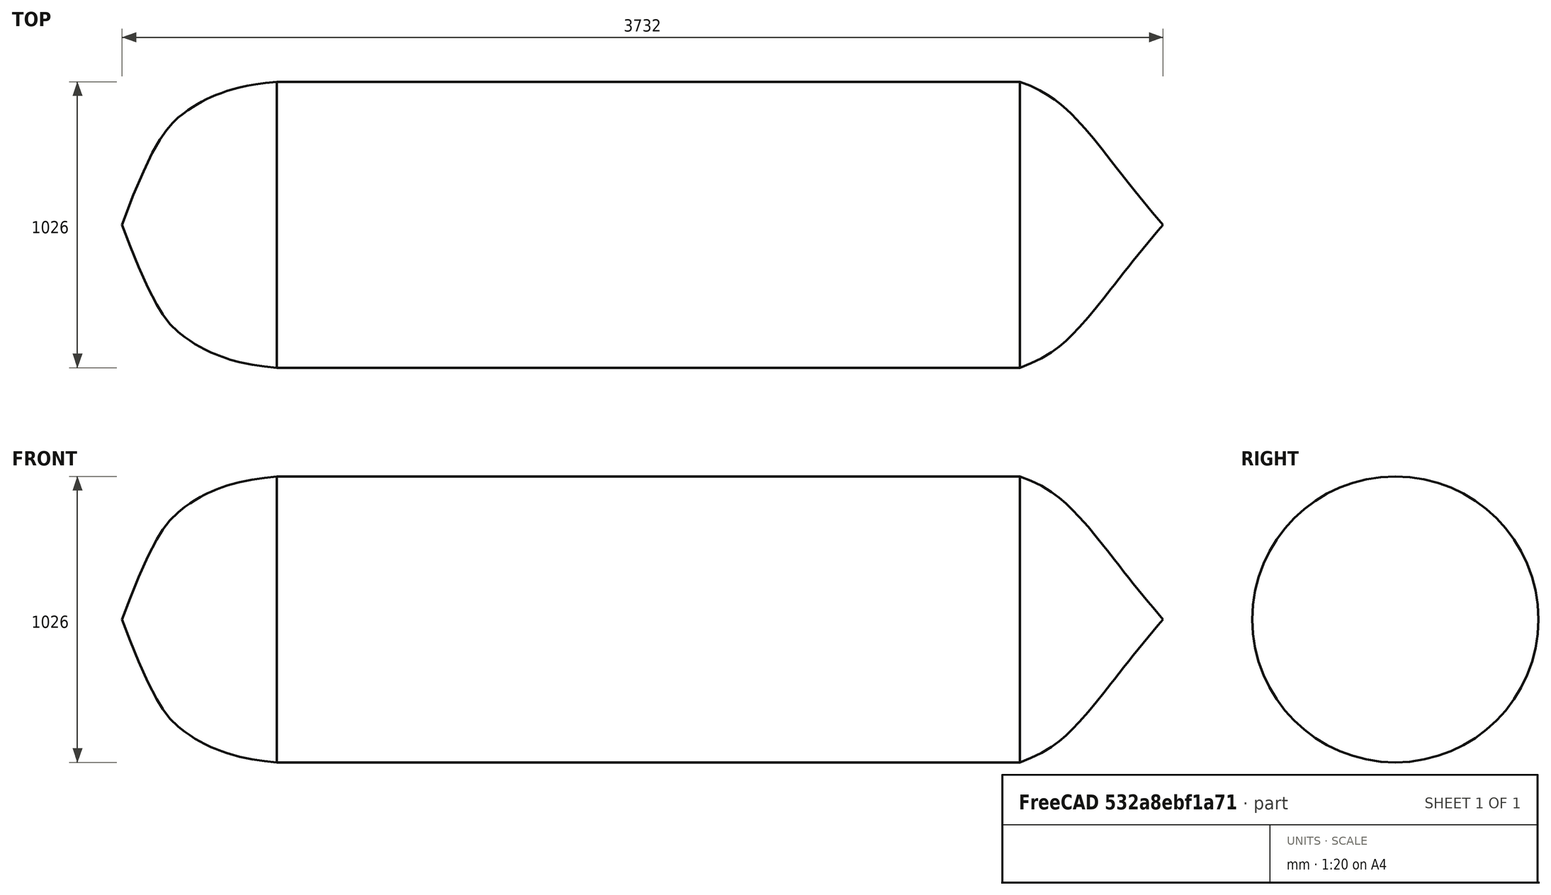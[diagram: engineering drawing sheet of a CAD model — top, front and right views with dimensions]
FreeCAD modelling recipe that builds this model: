
FCSTD DOCUMENT  (FreeCAD 0.19R24291 (Git))
Label: Remus_Myring_hull
License: All rights reserved
LicenseURL: http://en.wikipedia.org/wiki/All_rights_reserved
objects: Sketcher::SketchObject×1, PartDesign::Revolution×1, PartDesign::Body×1, TechDraw::DrawSVGTemplate×1, TechDraw::DrawViewPart×1, TechDraw::DrawViewSection×1, TechDraw::DrawPage×1
note: 4 computed .brp shape members not serialized (recipe doc carries the construction recipe); baked Part::Feature solids carry a one-line shape summary decoded from their .brp

FEATURE [Sketcher::SketchObject] Sketch
  FullyConstrained = true
  MapMode = 5
  Support = -> [XY_Plane]
  expr: .Constraints.tail3_x = .Constraints.myring_c * 3 / 5
  expr: .Constraints.tail4_x = .Constraints.myring_c * 4 / 5
  expr: .Constraints.tail1_x = .Constraints.myring_c * 1 / 5
  expr: .Constraints.tail2_x = .Constraints.myring_c * 2 / 5
  expr: .Constraints.nose4_x = .Constraints.myring_a * 4 / 5
  expr: .Constraints.nose3_x = .Constraints.myring_a * 3 / 5
  expr: .Constraints.nose2_x = .Constraints.myring_a * 2 / 5
  expr: .Constraints.nose1_x = .Constraints.myring_a * 1 / 5
  expr: Constraints[5] = .Constraints.myring_r
  expr: .Constraints.body1_x = .Constraints.myring_b * 1 / 6
  expr: .Constraints.body4_x = .Constraints.myring_b * 4 / 6
  expr: .Constraints.body2_x = .Constraints.myring_b * 2 / 6
  expr: .Constraints.body3_x = .Constraints.myring_b * 3 / 6
  expr: .Constraints.body5_x = .Constraints.myring_b * 5 / 6
  sketch-geometry (36):
    g0: LineSegment StartX=1332 StartY=513 StartZ=0 EndX=1332 EndY=0 EndZ=0
    g1: LineSegment StartX=-1332 StartY=513 StartZ=0 EndX=-1332 EndY=0 EndZ=0
    g2: LineSegment StartX=-1332 StartY=0 StartZ=0 EndX=1332 EndY=0 EndZ=0
    g3: LineSegment StartX=-1332 StartY=0 StartZ=0 EndX=-1887 EndY=0 EndZ=0
    g4: LineSegment StartX=1332 StartY=0 StartZ=0 EndX=1845 EndY=0 EndZ=0
    g5-g10: Circle x6 (B-spline internal-alignment scaffolding for g11; pole/knot coordinates omitted)
    g11: BSplineCurve PolesCount=6 KnotsCount=4 Degree=3 IsPeriodic=0
    g12-g15: GeomPoint x4 (B-spline internal-alignment scaffolding for g11; pole/knot coordinates omitted)
    g16-g22: Circle x7 (B-spline internal-alignment scaffolding for g23; pole/knot coordinates omitted)
    g23: BSplineCurve PolesCount=7 KnotsCount=5 Degree=3 IsPeriodic=0
    g24: GeomPoint X=-1332 Y=513 Z=0
    g25: GeomPoint X=1332 Y=513 Z=0
    g26-g31: Circle x6 (B-spline internal-alignment scaffolding for g32; pole/knot coordinates omitted)
    g32: BSplineCurve PolesCount=6 KnotsCount=4 Degree=3 IsPeriodic=0
    g33: GeomPoint X=1332 Y=513 Z=0
    g34: GeomPoint X=1648.35 Y=243.281 Z=0
    g35: GeomPoint X=1845 Y=0 Z=0
  constraints (62):
    c: Vertical(g0)
    c: Vertical(g1)
    c: DistanceX(g1,g0) = 2664  'myring_b'
    c: Symmetric(g1,g0,g-2)
    c: DistanceY(g0,g0) = 513  'myring_r'
    c: DistanceY(g1,g1) = 513
    c: Coincident(g2,g1)
    c: Coincident(g2,g0)
    c: Coincident(g3,g1)
    c: PointOnObject(g3,g-1)
    c: Horizontal(g3)
    c: Coincident(g4,g0)
    c: PointOnObject(g4,g-1)
    c: DistanceX(g3,g2) = 555  'myring_a'
    c: DistanceX(g2,g4) = 513  'myring_c'
    c: Coincident(g11,g3)
    c: Weight(g5) = 1
    c: Equal(g5, g6-g10) x5
    c: Coincident(g11,g1)
    c: InternalAlignment(g5-g10 -> g11) x6
    c: InternalAlignment(g12-g15 -> g11) x4
    c: Coincident(g23,g11)
    c: Weight(g16) = 1
    c: Equal(g16, g17-g22) x6
    c: Coincident(g23,g0)
    c: InternalAlignment(g16-g22 -> g23) x7
    c: InternalAlignment(g24,g23)
    c: InternalAlignment(g25,g23)
    c: Coincident(g32,g23)
    c: Weight(g26) = 1
    c: Equal(g26, g27-g31) x5
    c: Coincident(g32,g4)
    c: InternalAlignment(g26-g31 -> g32) x6
    c: InternalAlignment(g33,g32)
    c: InternalAlignment(g34,g32)
    c: InternalAlignment(g35,g32)
    c: DistanceY(g3,g6) = 306.216  'nose1_y'
    c: DistanceY(g3,g7) = 409.47  'nose2_y'
    c: DistanceY(g3,g8) = 469.75  'nose3_y'
    c: DistanceY(g3,g9) = 502.53  'nose4_y'
    c: DistanceX(g3,g6) = 111  'nose1_x'
    c: DistanceX(g3,g7) = 222  'nose2_x'
    c: DistanceX(g3,g8) = 333  'nose3_x'
    c: DistanceX(g3,g9) = 444  'nose4_x'
    c: DistanceY(g2,g27) = 476.42  'tail1_y'
    c: DistanceY(g2,g28) = 382.75  'tail2_y'
    c: DistanceY(g2,g29) = 256.07  'tail3_y'
    c: DistanceY(g2,g30) = 120.46  'tail4_y'
    c: DistanceX(g2,g27) = 102.6  'tail1_x'
    c: DistanceX(g2,g28) = 205.2  'tail2_x'
    c: DistanceX(g2,g29) = 307.8  'tail3_x'
    c: DistanceX(g2,g30) = 410.4  'tail4_x'
    c: DistanceX(g11,g17) = 444  'body1_x'
    c: DistanceX(g11,g18) = 888  'body2_x'
    c: DistanceX(g11,g19) = 1332  'body3_x'
    c: DistanceX(g11,g20) = 1776  'body4_x'
    c: DistanceX(g11,g21) = 2220  'body5_x'
    c: DistanceY(g11,g17) = 0  'body1_y'
    c: DistanceY(g11,g18) = 0  'body2_y'
    c: DistanceY(g11,g19) = 0  'body3_y'
    c: DistanceY(g11,g20) = 0  'body4_y'
    c: DistanceY(g11,g21) = 0  'body5_y'
FEATURE [PartDesign::Revolution] Revolution
  Angle = 360
  Axis = (1,0,0)
  Base = (0,0,0)
  Profile = -> Sketch
  ReferenceAxis = -> Sketch [H_Axis]
FEATURE [PartDesign::Body] Body
  Group = -> [Sketch,Revolution]
  Origin = -> Origin
  Tip = -> Revolution
FEATURE [TechDraw::DrawSVGTemplate] Template
  EditableTexts = Designed_by_Name=Designed by Name; Drawing_number=Drawing number; FC-Date=Date; FC-SC=Scale; FC-SH=Sheet; FC-Title=Title; Subtitle=Subtitle; Weight=Weight
  Height = 210
  Orientation = 1
  Width = 297
FEATURE [TechDraw::DrawViewPart] View
  CoarseView = false
  Direction = (0,0,1)
  Focus = 100
  HardHidden = false
  IsoCount = 0
  IsoHidden = false
  IsoVisible = false
  LockPosition = false
  Perspective = false
  Rotation = 0
  Scale = 0.05
  ScaleType = 0
  SeamHidden = false
  SeamVisible = true
  SmoothHidden = false
  SmoothVisible = true
  Source = -> [Body]
  X = 65.7614
  XDirection = (1,0,0)
  Y = 42.7117
FEATURE [TechDraw::DrawViewSection] SectionView  label="Section  - "
  BaseView = -> View
  CoarseView = false
  CutSurfaceDisplay = 2
  Direction = (0,1,0)
  FileGeomPattern = <path>
  FileHatchPattern = <path>
  Focus = 100
  FuseBeforeCut = false
  HardHidden = false
  HatchScale = 1
  IsoCount = 0
  IsoHidden = false
  IsoVisible = false
  LockPosition = false
  NameGeomPattern = Diamond
  Perspective = false
  Rotation = 0
  Scale = 0.1
  ScaleType = 0
  SeamHidden = false
  SeamVisible = true
  SectionDirection = 3
  SectionNormal = (0,1,0)
  SectionOrigin = (0,0,0)
  SmoothHidden = false
  SmoothVisible = true
  Source = -> [Body]
  X = 144.754
  XDirection = (1,0,0)
  Y = 127.102
FEATURE [TechDraw::DrawPage] Page
  KeepUpdated = true
  NextBalloonIndex = 1
  ProjectionType = 0
  Template = -> Template
  Views = -> [View,SectionView]
note: 2 file-system paths scrubbed to <path> (originals preserved in the JSON sidecar)
